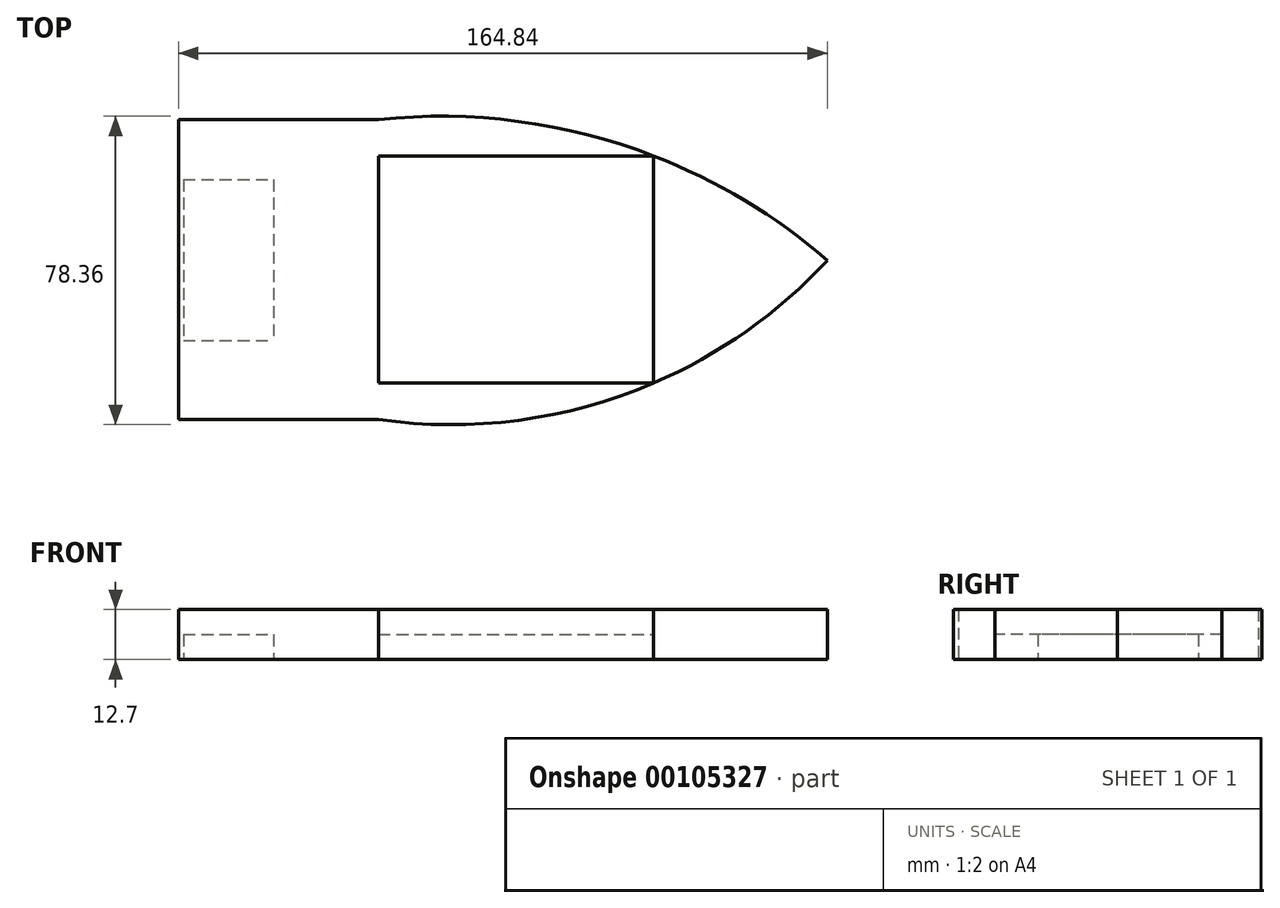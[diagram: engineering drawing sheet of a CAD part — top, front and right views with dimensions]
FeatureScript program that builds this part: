
annotation { "Feature Type Name" : "Feature", "Feature Type Description" : "" }
export const myFeature = defineFeature(function(context is Context, id is Id, definition is map)
    precondition{}
    {
        {
            var Q0;
            Q0=qCreatedBy(makeId("Top.planeOp"),FACE);
            var sketch = newSketch(context, id + "F0", { "sketchPlane" : qUnion([Q0])});
            skLineSegment(sketch, "E0.bottom", {"start": v(-91.53, 35.77) * mm, "end": v(-40.73, 35.77) * mm});
            skLineSegment(sketch, "E0.top", {"start": v(-91.53, -40.43) * mm, "end": v(-40.73, -40.43) * mm});
            skLineSegment(sketch, "E0.left", {"start": v(-91.53, 35.77) * mm, "end": v(-91.53, -40.43) * mm});
            skLineSegment(sketch, "E0.right", {"start": v(-40.73, 35.77) * mm, "end": v(-40.73, -40.43) * mm});
            skPoint(sketch, "E1", {"position": v(-90.26, 20.53) * mm});
            skPoint(sketch, "E2", {"position": v(-90.26, -25.19) * mm});
            skLineSegment(sketch, "E3.bottom", {"start": v(-90.26, 20.53) * mm, "end": v(-67.4, 20.53) * mm});
            skLineSegment(sketch, "E3.top", {"start": v(-90.26, -20.31) * mm, "end": v(-67.4, -20.31) * mm});
            skLineSegment(sketch, "E3.left", {"start": v(-90.26, 20.53) * mm, "end": v(-90.26, -20.31) * mm});
            skLineSegment(sketch, "E3.right", {"start": v(-67.4, 20.53) * mm, "end": v(-67.4, -20.31) * mm});
            skLineSegment(sketch, "E4.bottom", {"start": v(-40.73, 26.53) * mm, "end": v(29.12, 26.53) * mm});
            skLineSegment(sketch, "E4.top", {"start": v(-40.73, -31.22) * mm, "end": v(29.12, -31.22) * mm});
            skLineSegment(sketch, "E4.left", {"start": v(-40.73, 26.53) * mm, "end": v(-40.73, -31.22) * mm});
            skLineSegment(sketch, "E4.right", {"start": v(29.12, 26.53) * mm, "end": v(29.12, -31.22) * mm});
            skPoint(sketch, "E5.positionSnap0", {"position": v(-40.73, -2.33) * mm});
            skArc(sketch, "E6", {"start": v(73.31, 0) * mm, "mid": v(20, 29.71) * mm, "end": v(-40.73, 35.77) * mm});
            skArc(sketch, "E7", {"start": v(-40.73, -40.43) * mm, "mid": v(21.28, -34.29) * mm, "end": v(73.31, 0) * mm});
            skSolve(sketch);
        }
        {
            var Q0;
            {var subQ1=sQuery(id+"F0.wireOp",EDGE,"E0.bottom");Q0=makeQuery(id+"F0.imprint","IMPRINT",FACE,{"disambiguationData":[TD([[makeQuery(id+"F0.imprint","IMPRINT",EDGE,{"derivedFrom":subQ1}),-1.0]])]});}
            var Q1;
            {var subQ3=sQuery(id+"F0.wireOp",EDGE,"E4.bottom");Q1=makeQuery(id+"F0.imprint","IMPRINT",FACE,{"disambiguationData":[TD([[makeQuery(id+"F0.imprint","IMPRINT",EDGE,{"derivedFrom":subQ3}),1.0]])]});}
            var Q2;
            {var subQ0=sQuery(id+"F0.wireOp",EDGE,"E4.right");Q2=makeQuery(id+"F0.imprint","IMPRINT",FACE,{"disambiguationData":[TD([[makeQuery(id+"F0.imprint","IMPRINT",EDGE,{"derivedFrom":subQ0}),1.0]])]});}
            var Q3;
            {var subQ3=sQuery(id+"F0.wireOp",EDGE,"E4.top");Q3=makeQuery(id+"F0.imprint","IMPRINT",FACE,{"disambiguationData":[TD([[makeQuery(id+"F0.imprint","IMPRINT",EDGE,{"derivedFrom":subQ3}),-1.0]])]});}
            extrude(context, id + "F1", {"entities" : qUnion([Q0, Q1, Q2, Q3]), "endBound" : BoundingType.SYMMETRIC, "depth" : 12.7 * mm});
        }
        {
            var Q0;
            Q0=makeQuery(id+"F0.imprint","IMPRINT",FACE,{"disambiguationData":[TD([[makeQuery(id+"F0.imprint","IMPRINT",EDGE,{"derivedFrom":sQuery(id+"F0.wireOp",EDGE,"E3.bottom")}),-1.0]])]});
            extrude(context, id + "F2", {"entities" : qUnion([Q0]), "operationType" : NewBodyOperationType.ADD, "depth" : 6.35 * mm});
        }
        {
            var Q0;
            Q0=makeQuery(id+"F0.imprint","IMPRINT",FACE,{"disambiguationData":[TD([[makeQuery(id+"F0.imprint","IMPRINT",EDGE,{"derivedFrom":sQuery(id+"F0.wireOp",EDGE,"E4.bottom")}),-1.0]])]});
            extrude(context, id + "F3", {"entities" : qUnion([Q0]), "depth" : 6.35 * mm});
        }
    });
